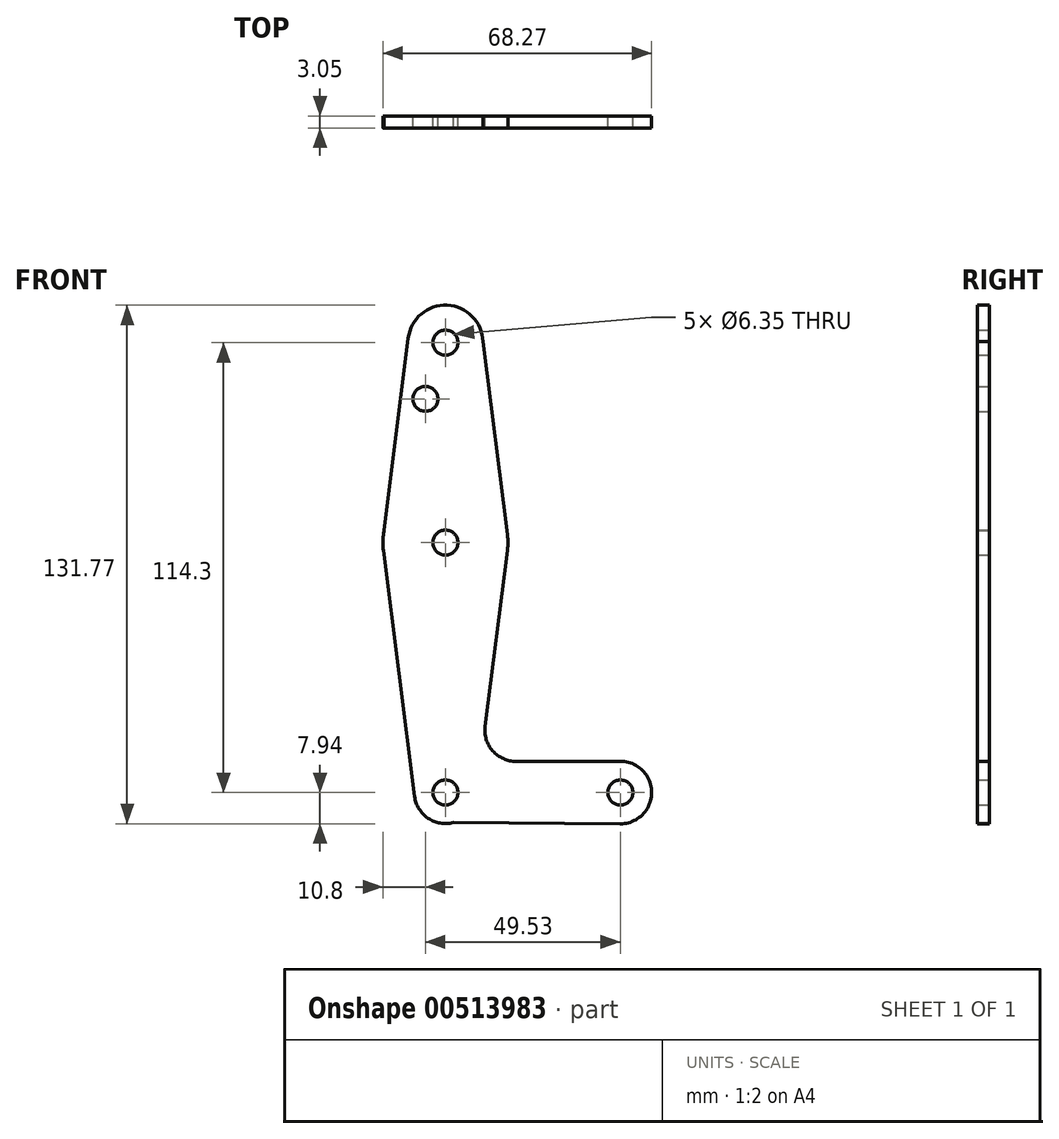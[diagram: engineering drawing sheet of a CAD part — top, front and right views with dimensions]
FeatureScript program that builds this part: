
annotation { "Feature Type Name" : "Feature", "Feature Type Description" : "" }
export const myFeature = defineFeature(function(context is Context, id is Id, definition is map)
    precondition{}
    {
        {
            var Q0;
            Q0=qCreatedBy(makeId("Front.planeOp"),FACE);
            var sketch = newSketch(context, id + "F0", { "sketchPlane" : qUnion([Q0])});
            skLineSegment(sketch, "E0", {"start": v(0, 0) * mm, "end": v(0, 114.3) * mm, "construction": true});
            skCircle(sketch, "E1", {"center": v(0, 63.5) * mm, "radius": 15.88 * mm});
            skCircle(sketch, "E2", {"center": v(0, 114.3) * mm, "radius": 9.53 * mm});
            skCircle(sketch, "E3", {"center": v(0, 0) * mm, "radius": 7.88 * mm});
            skLineSegment(sketch, "E4", {"start": v(0, 0) * mm, "end": v(44.45, 0) * mm, "construction": true});
            skCircle(sketch, "E5", {"center": v(44.45, 0) * mm, "radius": 7.94 * mm});
            skLineSegment(sketch, "E6", {"start": v(-15.85, 64.32) * mm, "end": v(-9.45, 115.48) * mm});
            skLineSegment(sketch, "E7", {"start": v(9.52, 114.56) * mm, "end": v(15.75, 65.5) * mm});
            skLineSegment(sketch, "E8", {"start": v(2, -7.62) * mm, "end": v(45.6, -7.95) * mm});
            skCircle(sketch, "E9", {"center": v(0, 114.3) * mm, "radius": 3.18 * mm});
            skCircle(sketch, "E10", {"center": v(-5.08, 100.03) * mm, "radius": 3.18 * mm});
            skCircle(sketch, "E11", {"center": v(0, 63.5) * mm, "radius": 3.18 * mm});
            skCircle(sketch, "E12", {"center": v(44.45, 0) * mm, "radius": 3.18 * mm});
            skCircle(sketch, "E13", {"center": v(0, 0) * mm, "radius": 3.18 * mm});
            skLineSegment(sketch, "E14", {"start": v(-15.75, 61.5) * mm, "end": v(-7.82, -1) * mm});
            skLineSegment(sketch, "E15", {"start": v(15.75, 61.5) * mm, "end": v(10.08, 16.85) * mm});
            skLineSegment(sketch, "E16", {"start": v(44.44, 7.94) * mm, "end": v(17.98, 7.9) * mm});
            skArc(sketch, "E17.filletArc", {"start": v(10.08, 16.85) * mm, "mid": v(12, 10.6) * mm, "end": v(17.98, 7.9) * mm});
            skSolve(sketch);
        }
        {
            var Q0;
            Q0 = qSketchRegion(id + "F0", true);
            extrude(context, id + "F1", {"entities" : qUnion([Q0]), "depth" : 3.05 * mm, "offsetDistance" : 25.4 * mm});
        }
    });
